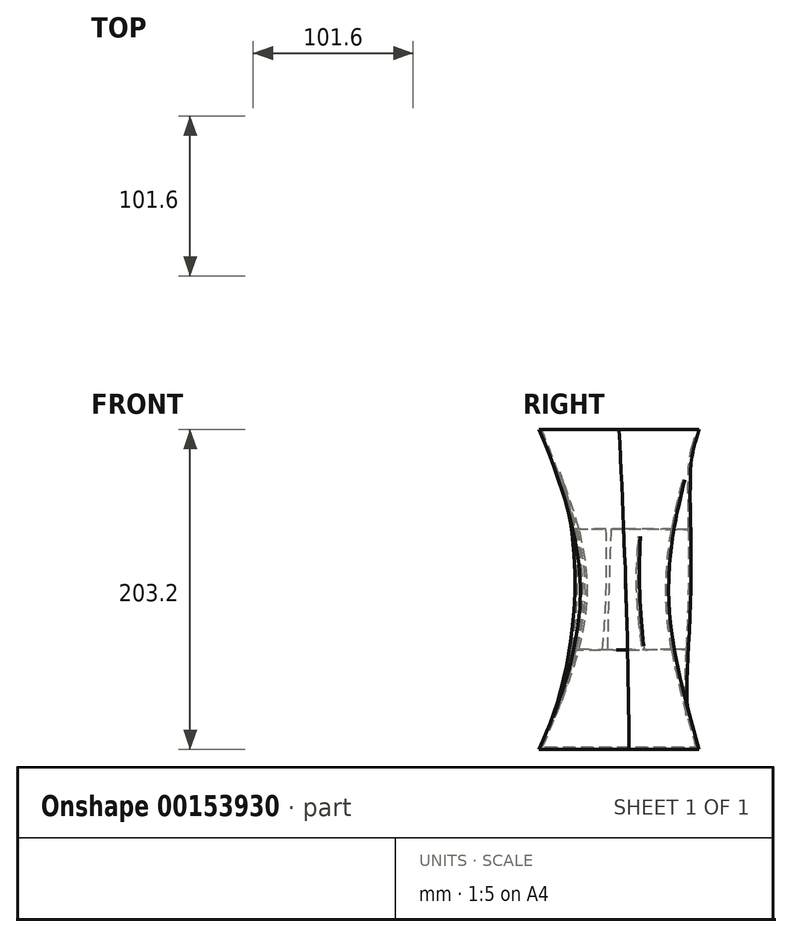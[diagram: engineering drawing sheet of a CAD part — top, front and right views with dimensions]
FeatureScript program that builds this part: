
annotation { "Feature Type Name" : "Feature", "Feature Type Description" : "" }
export const myFeature = defineFeature(function(context is Context, id is Id, definition is map)
    precondition{}
    {
        {
            var Q0;
            Q0=qCreatedBy(makeId("Top.planeOp"),FACE);
            var sketch = newSketch(context, id + "F0", { "sketchPlane" : qUnion([Q0])});
            skCircle(sketch, "E0", {"center": v(0, 0) * mm, "radius": 50.8 * mm});
            skSolve(sketch);
        }
        {
            var Q0;
            Q0=qCreatedBy(makeId("Top.planeOp"),FACE);
            cPlane(context, id + "F1", {"entities" : qUnion([Q0]), "cplaneType" : CPlaneType.OFFSET, "offset" : 101.6 * mm, "width" : 152.4 * mm, "height" : 152.4 * mm});
        }
        {
            var Q0;
            Q0=qCreatedBy(id+"F1.planeOp",FACE);
            var sketch = newSketch(context, id + "F2", { "sketchPlane" : qUnion([Q0])});
            skFitSpline(sketch, "E1", {"points": [v(-17.71, 44.38) * mm, v(-30.5, 18.8) * mm, v(-25.4, 8.76) * mm, v(-33.85, -8.37) * mm, v(-31.89, -9.74) * mm, v(-20.47, -15.25) * mm, v(-17.52, -26.08) * mm, v(-7.48, -27.46) * mm, v(0, -23.91) * mm, v(6.5, -21.36) * mm, v(15.16, -24.5) * mm, v(18.5, -22.34) * mm, v(18.9, -17.22) * mm, v(13.97, -14.07) * mm, v(14.76, -9.55) * mm, v(19.68, -5.02) * mm, v(25.78, -3.05) * mm, v(34.05, 3.84) * mm, v(33.26, 7.18) * mm, v(26.77, 13.09) * mm, v(22.64, 12.5) * mm, v(19.1, 17.81) * mm, v(21.45, 22.14) * mm, v(22.24, 23.72) * mm, v(20.67, 27.26) * mm, v(13.19, 31.4) * mm, v(5.31, 31.4) * mm, v(1.38, 38.68) * mm, v(-17.71, 44.38) * mm]});
            skSolve(sketch);
        }
        {
            var Q0;
            Q0=qCreatedBy(id+"F1.planeOp",FACE);
            cPlane(context, id + "F3", {"entities" : qUnion([Q0]), "cplaneType" : CPlaneType.OFFSET, "offset" : 101.6 * mm, "width" : 152.4 * mm, "height" : 152.4 * mm});
        }
        {
            var Q0;
            Q0=qCreatedBy(id+"F3.planeOp",FACE);
            var sketch = newSketch(context, id + "F4", { "sketchPlane" : qUnion([Q0])});
            skCircle(sketch, "E2", {"center": v(0, 0) * mm, "radius": 50.8 * mm});
            skSolve(sketch);
        }
        {
            var Q0;
            Q0=makeQuery(id+"F4.imprint","IMPRINT",FACE,{"disambiguationData":[TD([[makeQuery(id+"F4.imprint","IMPRINT",EDGE,{"derivedFrom":sQuery(id+"F4.wireOp",EDGE,"E2")}),1.0]])]});
            var Q1;
            Q1=makeQuery(id+"F2.imprint","IMPRINT",FACE,{"disambiguationData":[TD([[makeQuery(id+"F2.imprint","IMPRINT",EDGE,{"derivedFrom":sQuery(id+"F2.wireOp",EDGE,"E1")}),1.0]])]});
            var Q2;
            Q2=makeQuery(id+"F0.imprint","IMPRINT",FACE,{"disambiguationData":[TD([[makeQuery(id+"F0.imprint","IMPRINT",EDGE,{"derivedFrom":sQuery(id+"F0.wireOp",EDGE,"E0")}),1.0]])]});
            loft(context, id + "F5", {"sheetProfilesArray" : [{ "sheetProfileEntities" : qUnion([Q0]) }, { "sheetProfileEntities" : qUnion([Q1]) }, { "sheetProfileEntities" : qUnion([Q2]) }]});
        }
        {
            var Q0;
            Q0=makeQuery(id+"F5.opLoft","CAP_FACE",FACE,{"disambiguationData":[OSD([makeQuery(id+"F4.imprint","IMPRINT",FACE,{"disambiguationData":[TD([[makeQuery(id+"F4.imprint","IMPRINT",EDGE,{"derivedFrom":sQuery(id+"F4.wireOp",EDGE,"E2")}),1.0]])]})])],"isStart":true});
            shell(context, id + "F6", {"entities" : qUnion([Q0]), "thickness" : 1.27 * mm});
        }
    });
